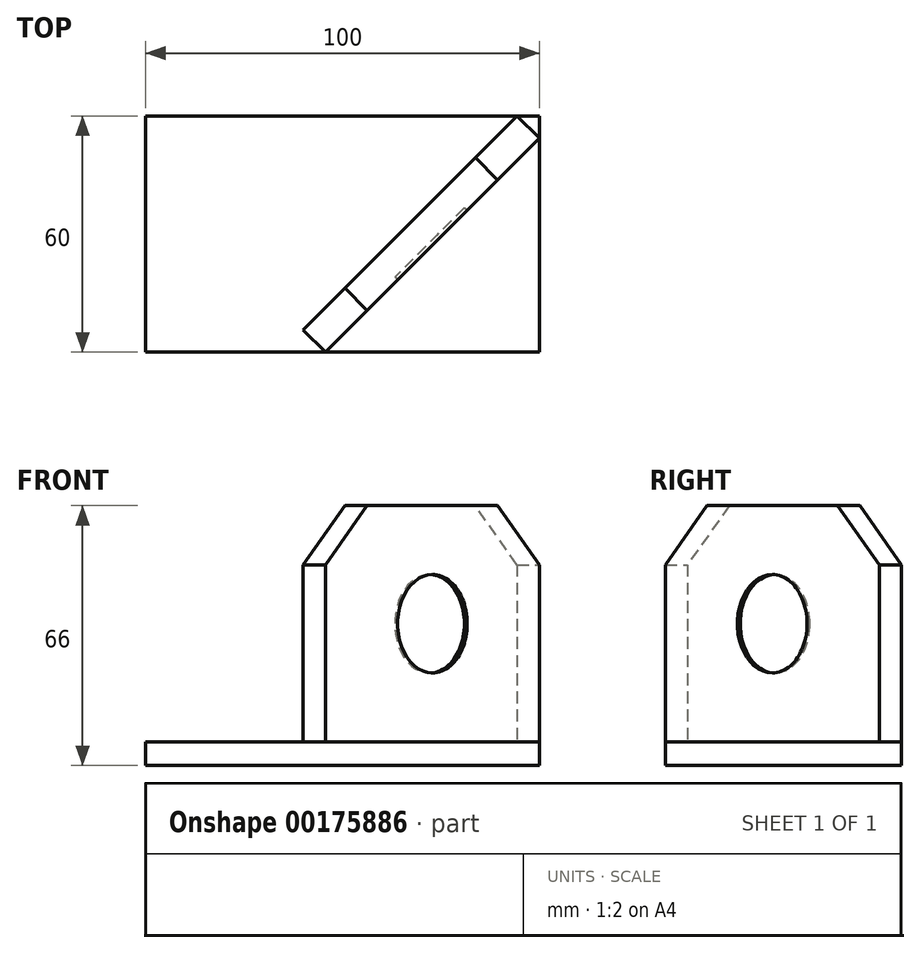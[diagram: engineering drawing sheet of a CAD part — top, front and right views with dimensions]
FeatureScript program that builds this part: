
annotation { "Feature Type Name" : "Feature", "Feature Type Description" : "" }
export const myFeature = defineFeature(function(context is Context, id is Id, definition is map)
    precondition{}
    {
        {
            var Q0;
            Q0=qCreatedBy(makeId("Top.planeOp"),FACE);
            var sketch = newSketch(context, id + "F0", { "sketchPlane" : qUnion([Q0])});
            skLineSegment(sketch, "E0.bottom", {"start": v(-50, 30) * mm, "end": v(50, 30) * mm});
            skLineSegment(sketch, "E0.top", {"start": v(-50, -30) * mm, "end": v(50, -30) * mm});
            skLineSegment(sketch, "E0.left", {"start": v(-50, 30) * mm, "end": v(-50, -30) * mm});
            skLineSegment(sketch, "E0.right", {"start": v(50, 30) * mm, "end": v(50, -30) * mm});
            skPoint(sketch, "E0.middle", {"position": v(0, 0) * mm});
            skSolve(sketch);
        }
        {
            var Q0;
            Q0 = qSketchRegion(id + "F0", true);
            extrude(context, id + "F1", {"entities" : qUnion([Q0]), "depth" : 6 * mm});
        }
        {
            var Q0;
            Q0=makeQuery(id+"F1.opExtrude","CAP_FACE",FACE,{"disambiguationData":[OSD([sQuery(id+"F0.wireOp",EDGE,"E0.bottom"),sQuery(id+"F0.wireOp",EDGE,"E0.top"),sQuery(id+"F0.wireOp",EDGE,"E0.left"),sQuery(id+"F0.wireOp",EDGE,"E0.right")])],"isStart":false});
            var sketch = newSketch(context, id + "F2", { "sketchPlane" : qUnion([Q0])});
            skLineSegment(sketch, "E1", {"start": v(-10, -24.34) * mm, "end": v(44.34, 30) * mm});
            skLineSegment(sketch, "E2", {"start": v(44.34, 30) * mm, "end": v(50, 24.34) * mm});
            skLineSegment(sketch, "E3", {"start": v(50, 24.34) * mm, "end": v(-4.34, -30) * mm});
            skLineSegment(sketch, "E4", {"start": v(-4.34, -30) * mm, "end": v(-10, -24.34) * mm});
            skSolve(sketch);
        }
        {
            var Q0;
            Q0 = qSketchRegion(id + "F2", true);
            extrude(context, id + "F3", {"entities" : qUnion([Q0]), "operationType" : NewBodyOperationType.ADD, "depth" : 60 * mm});
        }
        {
            var Q0;
            Q0=makeQuery(id+"F3.opExtrude","SWEPT_FACE",FACE,{"disambiguationData":[OSD([sQuery(id+"F2.wireOp",EDGE,"E3")])]});
            var sketch = newSketch(context, id + "F4", { "sketchPlane" : qUnion([Q0])});
            skCircle(sketch, "E5", {"center": v(14.14, 36) * mm, "radius": 12.5 * mm});
            skSolve(sketch);
        }
        {
            var Q0;
            Q0 = qSketchRegion(id + "F4", true);
            extrude(context, id + "F5", {"entities" : qUnion([Q0]), "operationType" : NewBodyOperationType.REMOVE, "oppositeDirection" : true, "depth" : 1 * mm});
        }
        {
            var Q0;
            Q0=makeQuery(id+"F3.opExtrude","CAP_EDGE",EDGE,{"disambiguationData":[OSD([sQuery(id+"F2.wireOp",EDGE,"E4")])],"isStart":false});
            var Q1;
            Q1=makeQuery(id+"F3.opExtrude","CAP_EDGE",EDGE,{"disambiguationData":[OSD([sQuery(id+"F2.wireOp",EDGE,"E2")])],"isStart":false});
            chamfer(context, id + "F6", {"entities" : qUnion([Q0, Q1]), "width" : 15 * mm, "tangentPropagation" : true});
        }
    });
